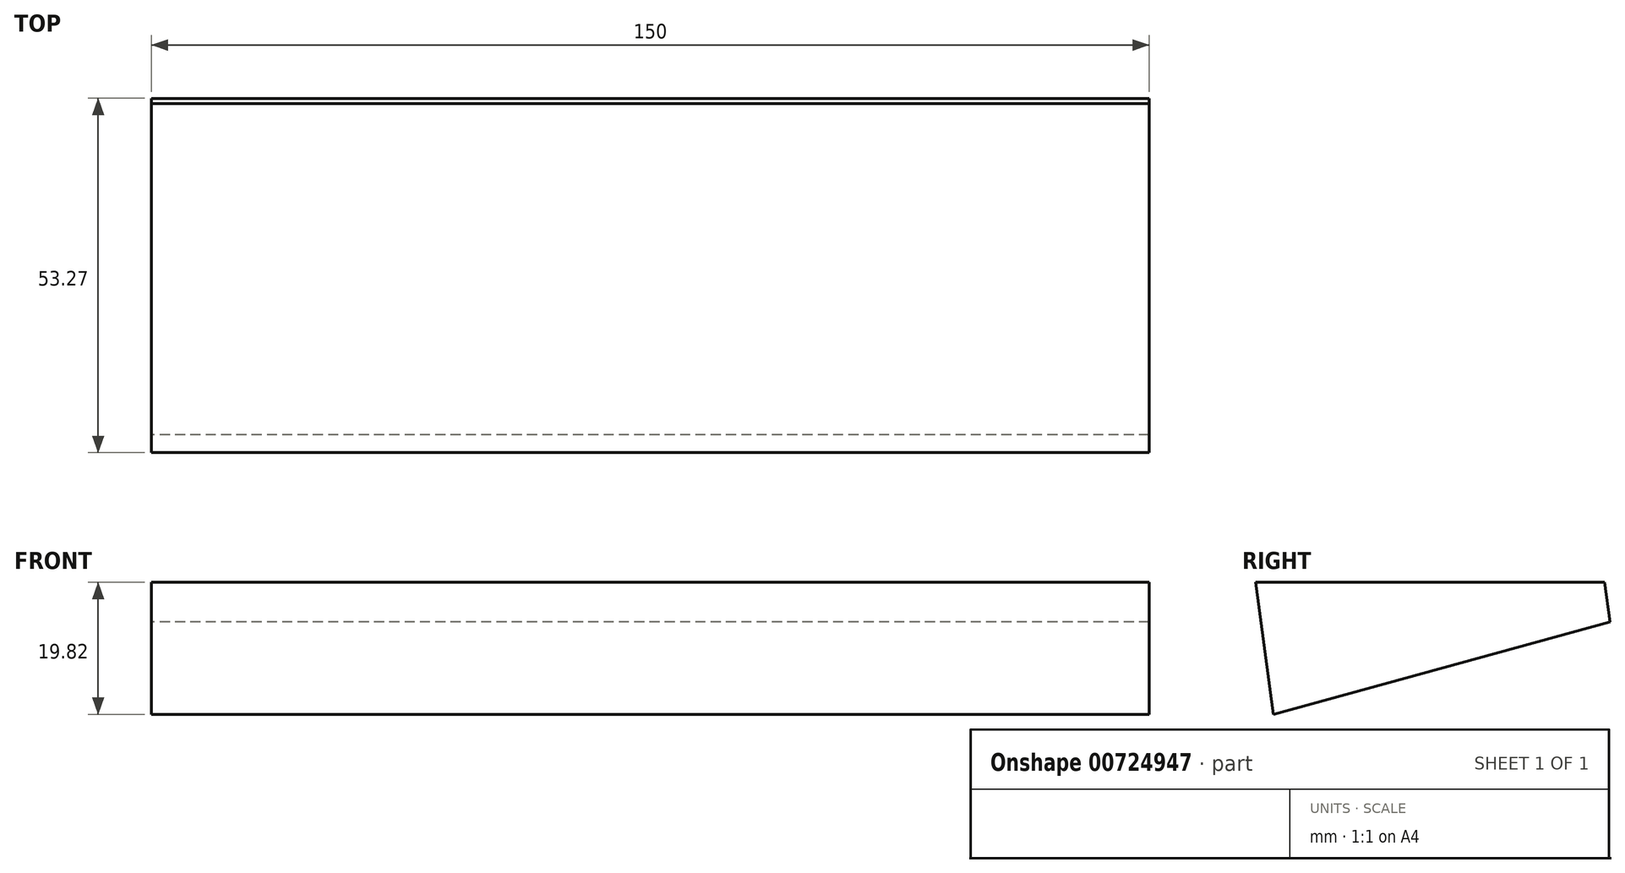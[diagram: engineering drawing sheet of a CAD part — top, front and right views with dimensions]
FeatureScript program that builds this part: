
annotation { "Feature Type Name" : "Feature", "Feature Type Description" : "" }
export const myFeature = defineFeature(function(context is Context, id is Id, definition is map)
    precondition{}
    {
        {
            var Q0;
            Q0=qCreatedBy(makeId("Right.planeOp"),FACE);
            var sketch = newSketch(context, id + "F0", { "sketchPlane" : qUnion([Q0])});
            skLineSegment(sketch, "E0", {"start": v(19.6, 23.1) * mm, "end": v(-31.93, 16.16) * mm, "construction": true});
            skLineSegment(sketch, "E1", {"start": v(-31.93, 16.16) * mm, "end": v(-33.26, 26.07) * mm});
            skLineSegment(sketch, "E2", {"start": v(-33.26, 26.07) * mm, "end": v(19.2, 26.07) * mm});
            skLineSegment(sketch, "E3", {"start": v(19.2, 26.07) * mm, "end": v(19.6, 23.1) * mm});
            skLineSegment(sketch, "E4.MirrorCS", {"start": v(20, 20.13) * mm, "end": v(19.6, 23.1) * mm});
            skLineSegment(sketch, "E5.MirrorCS", {"start": v(-30.6, 6.25) * mm, "end": v(20, 20.13) * mm});
            skLineSegment(sketch, "E6.MirrorCS", {"start": v(-31.93, 16.16) * mm, "end": v(-30.6, 6.25) * mm});
            skSolve(sketch);
        }
        {
            var Q0;
            Q0=makeQuery(id+"F0.imprint","IMPRINT",FACE,{"disambiguationData":[TD([[makeQuery(id+"F0.imprint","IMPRINT",EDGE,{"derivedFrom":sQuery(id+"F0.wireOp",EDGE,"E1")}),-1.0]])]});
            extrude(context, id + "F1", {"entities" : qUnion([Q0]), "depth" : 75 * mm, "offsetDistance" : 25.4 * mm, "hasSecondDirection" : true, "secondDirectionOppositeDirection" : true, "secondDirectionDepth" : 75 * mm});
        }
        {
            var Q0;
            Q0=makeQuery(id+"F1.opExtrude","SWEPT_FACE",FACE,{"disambiguationData":[OSD([sQuery(id+"F0.wireOp",EDGE,"E2")])]});
            var sketch = newSketch(context, id + "F2", { "sketchPlane" : qUnion([Q0])});
            skText(sketch, "E7", { "text": "Chancellor", "fontName": "OpenSans-Regular.ttf"});
            skLineSegment(sketch, "E8", {"start": v(-33.67, 19.2) * mm, "end": v(-33.67, 3.3) * mm, "construction": true});
            skLineSegment(sketch, "E9", {"start": v(-32.16, -17.35) * mm, "end": v(-32.16, -33.26) * mm, "construction": true});
            const initialGuessF2  = {"E7": [-0.072, 0.02294, 1, 0, 0.02065]};
            skSetInitialGuess(sketch, initialGuessF2);
            skSolve(sketch);
        }
        {
            var Q0;
            Q0=qSketchRegion(id+"F2",true);
            extrude(context, id + "F3", {"entities" : qUnion([Q0]), "operationType" : NewBodyOperationType.REMOVE, "oppositeDirection" : true, "depth" : 3 * mm, "offsetDistance" : 25 * mm});
        }
    });
